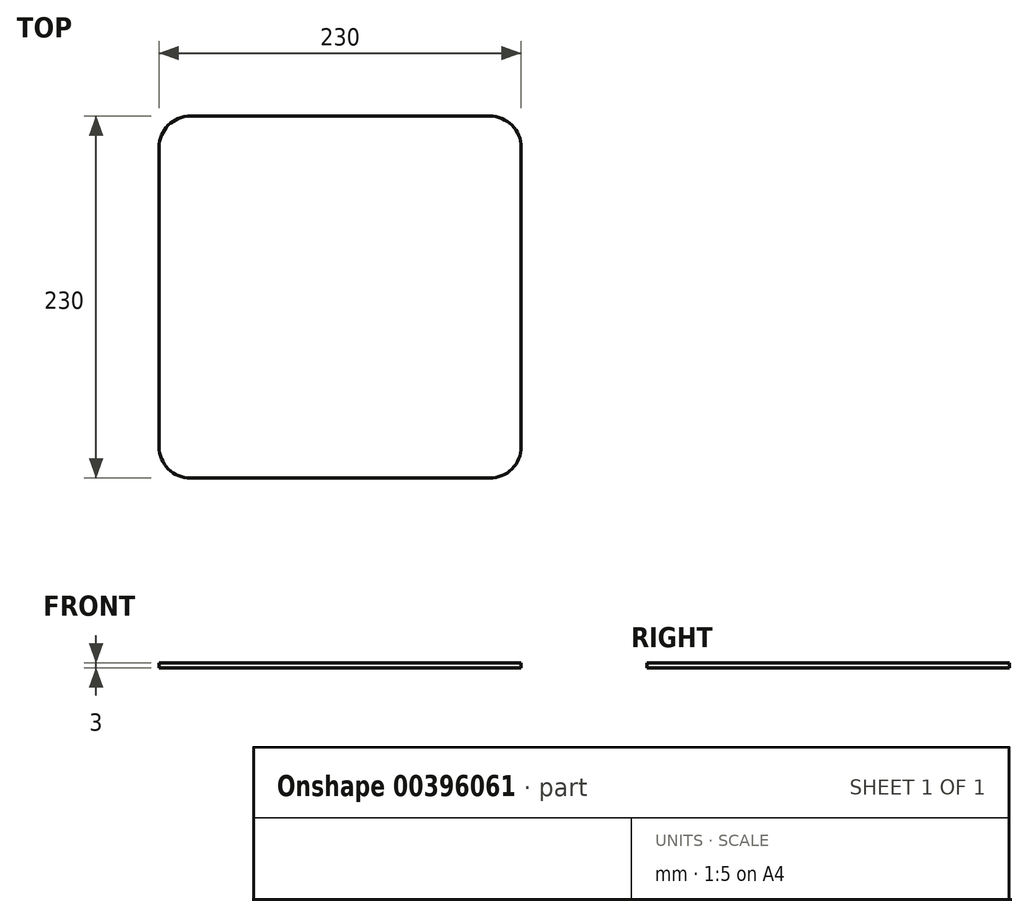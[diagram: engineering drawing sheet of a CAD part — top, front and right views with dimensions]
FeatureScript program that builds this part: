
annotation { "Feature Type Name" : "Feature", "Feature Type Description" : "" }
export const myFeature = defineFeature(function(context is Context, id is Id, definition is map)
    precondition{}
    {
        {
            var Q0;
            Q0=qCreatedBy(makeId("Top.planeOp"),FACE);
            var sketch = newSketch(context, id + "F0", { "sketchPlane" : qUnion([Q0])});
            skLineSegment(sketch, "E0.bottom", {"start": v(-95, 125) * mm, "end": v(95, 125) * mm});
            skLineSegment(sketch, "E0.top", {"start": v(-95, -105) * mm, "end": v(95, -105) * mm});
            skLineSegment(sketch, "E0.left", {"start": v(-115, 105) * mm, "end": v(-115, -85) * mm});
            skLineSegment(sketch, "E0.right", {"start": v(115, 105) * mm, "end": v(115, -85) * mm});
            skPoint(sketch, "E1.visualSharp", {"position": v(-115, 125) * mm});
            skArc(sketch, "E1.filletArc", {"start": v(-95, 125) * mm, "mid": v(-109.14, 119.14) * mm, "end": v(-115, 105) * mm});
            skPoint(sketch, "E2.visualSharp", {"position": v(-115, -105) * mm});
            skArc(sketch, "E2.filletArc", {"start": v(-115, -85) * mm, "mid": v(-109.14, -99.14) * mm, "end": v(-95, -105) * mm});
            skPoint(sketch, "E3.visualSharp", {"position": v(115, -105) * mm});
            skArc(sketch, "E3.filletArc", {"start": v(95, -105) * mm, "mid": v(109.14, -99.14) * mm, "end": v(115, -85) * mm});
            skPoint(sketch, "E4.visualSharp", {"position": v(115, 125) * mm});
            skArc(sketch, "E4.filletArc", {"start": v(115, 105) * mm, "mid": v(109.14, 119.14) * mm, "end": v(95, 125) * mm});
            skSolve(sketch);
        }
        {
            var Q0;
            Q0=qSketchRegion(id+"F0",true);
            extrude(context, id + "F1", {"entities" : qUnion([Q0]), "depth" : 3 * mm});
        }
    });
